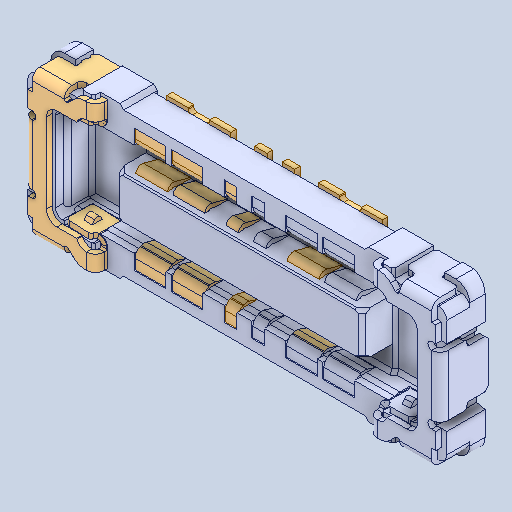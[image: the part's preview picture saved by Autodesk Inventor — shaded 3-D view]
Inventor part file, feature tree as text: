
AUTODESK INVENTOR PART (.ipt)
format: ipt  version: 2025 (Build 290162000, 162)  size: 939,520 bytes
history: native  units: mm
features: other x18, mirror x17
ambient origin geometry x8: Origin, YZ Plane, XZ Plane, XY Plane, X Axis, Y Axis, Z Axis, Center Point
bodies: Solid1 (feature_tree), Solid2 (feature_tree), Solid3 (feature_tree), Solid4 (feature_tree), Solid5 (feature_tree), Solid6 (feature_tree), Solid7 (feature_tree), Solid8 (feature_tree), Solid9 (feature_tree), Solid10 (feature_tree), Solid11 (feature_tree), Solid12 (feature_tree), Solid13 (feature_tree), Solid14 (feature_tree), Solid15 (feature_tree), Solid16 (feature_tree), Solid17 (feature_tree), Solid18 (feature_tree), Solid19 (feature_tree), Solid20 (feature_tree), Solid21 (feature_tree), Solid22 (feature_tree), Solid23 (feature_tree), Solid24 (feature_tree), Solid25 (feature_tree), Solid26 (feature_tree), Solid27 (feature_tree), Solid28 (feature_tree), Solid29 (feature_tree), Solid30 (feature_tree), Solid31 (feature_tree), Solid32 (feature_tree), Solid33 (feature_tree), Solid34 (feature_tree), Solid35 (feature_tree)
feature tree (35):
  mirror  "Mirror5[4]"
  mirror  "Mirror5[2]"
  other  "Boss-Extrude15"
  mirror  "Mirror5[5]"
  other  "Boss-Extrude11[4]"
  mirror  "Mirror5[6]"
  mirror  "Mirror5[3]"
  other  "Cut-Extrude9[2]"
  mirror  "Mirror5[9]"
  other  "Boss-Extrude14[1]"
  mirror  "Mirror5[10]"
  other  "Boss-Extrude12[1]"
  mirror  "Mirror5[7]"
  mirror  "Mirror5[11]"
  mirror  "Mirror4[4]"
  other  "Boss-Extrude13[2]"
  mirror  "Mirror5[1]"
  mirror  "Mirror2"
  other  "Boss-Extrude12[2]"
  mirror  "Mirror4[1]"
  other  "Boss-Extrude10[2]"
  other  "Boss-Extrude9[2]"
  other  "Boss-Extrude14[2]"
  other  "Boss-Extrude9[1]"
  other  "Cut-Extrude9[1]"
  other  "Boss-Extrude10[3]"
  other  "Boss-Extrude13[1]"
  other  "Boss-Extrude11[3]"
  other  "Cut-Extrude10"
  mirror  "Mirror5[12]"
  mirror  "Mirror4[2]"
  mirror  "Mirror4[3]"
  other  "LPattern1[1]"
  mirror  "Mirror5[8]"
  other  "LPattern1[3]"
